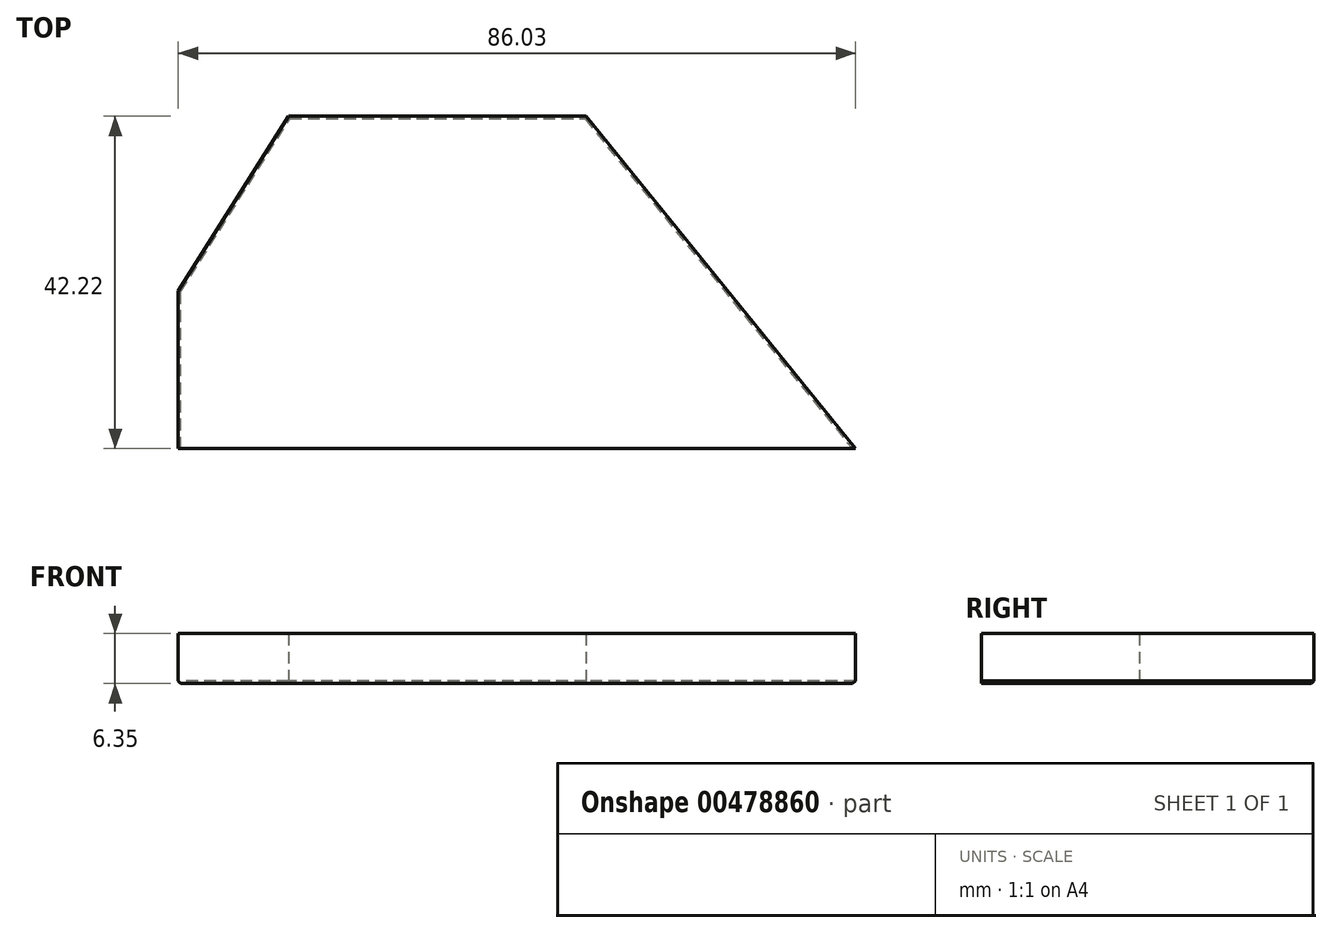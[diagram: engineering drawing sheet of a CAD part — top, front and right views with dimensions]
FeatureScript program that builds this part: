
annotation { "Feature Type Name" : "Feature", "Feature Type Description" : "" }
export const myFeature = defineFeature(function(context is Context, id is Id, definition is map)
    precondition{}
    {
        {
            var Q0;
            Q0=qCreatedBy(makeId("Top.planeOp"),FACE);
            var sketch = newSketch(context, id + "F0", { "sketchPlane" : qUnion([Q0])});
            skLineSegment(sketch, "E0", {"start": v(-41.06, 0) * mm, "end": v(44.97, 0) * mm});
            skLineSegment(sketch, "E1", {"start": v(10.74, 42.22) * mm, "end": v(44.97, 0) * mm});
            skLineSegment(sketch, "E2", {"start": v(10.74, 42.22) * mm, "end": v(-27.06, 42.22) * mm});
            skLineSegment(sketch, "E3", {"start": v(-41.06, 0) * mm, "end": v(-41.06, 20.04) * mm});
            skLineSegment(sketch, "E4", {"start": v(-41.06, 20.04) * mm, "end": v(-27.06, 42.22) * mm});
            skSolve(sketch);
        }
        {
            var Q0;
            Q0=makeQuery(id+"F0.imprint","IMPRINT",FACE,{"disambiguationData":[TD([[makeQuery(id+"F0.imprint","IMPRINT",EDGE,{"derivedFrom":sQuery(id+"F0.wireOp",EDGE,"E0")}),1.0]])]});
            extrude(context, id + "F1", {"entities" : qUnion([Q0]), "depth" : 6.35 * mm});
        }
        {
            var Q0;
            Q0=makeQuery(id+"F1.opExtrude","CAP_EDGE",EDGE,{"disambiguationData":[OSD([sQuery(id+"F0.wireOp",EDGE,"E1")])],"isStart":true});
            var Q1;
            Q1=makeQuery(id+"F1.opExtrude","CAP_EDGE",EDGE,{"disambiguationData":[OSD([sQuery(id+"F0.wireOp",EDGE,"E2")])],"isStart":true});
            var Q2;
            Q2=makeQuery(id+"F1.opExtrude","CAP_EDGE",EDGE,{"disambiguationData":[OSD([sQuery(id+"F0.wireOp",EDGE,"E4")])],"isStart":true});
            var Q3;
            Q3=makeQuery(id+"F1.opExtrude","CAP_EDGE",EDGE,{"disambiguationData":[OSD([sQuery(id+"F0.wireOp",EDGE,"E3")])],"isStart":true});
            chamfer(context, id + "F2", {"entities" : qUnion([Q0, Q1, Q2, Q3]), "width" : 0.32 * mm, "tangentPropagation" : true});
        }
    });
